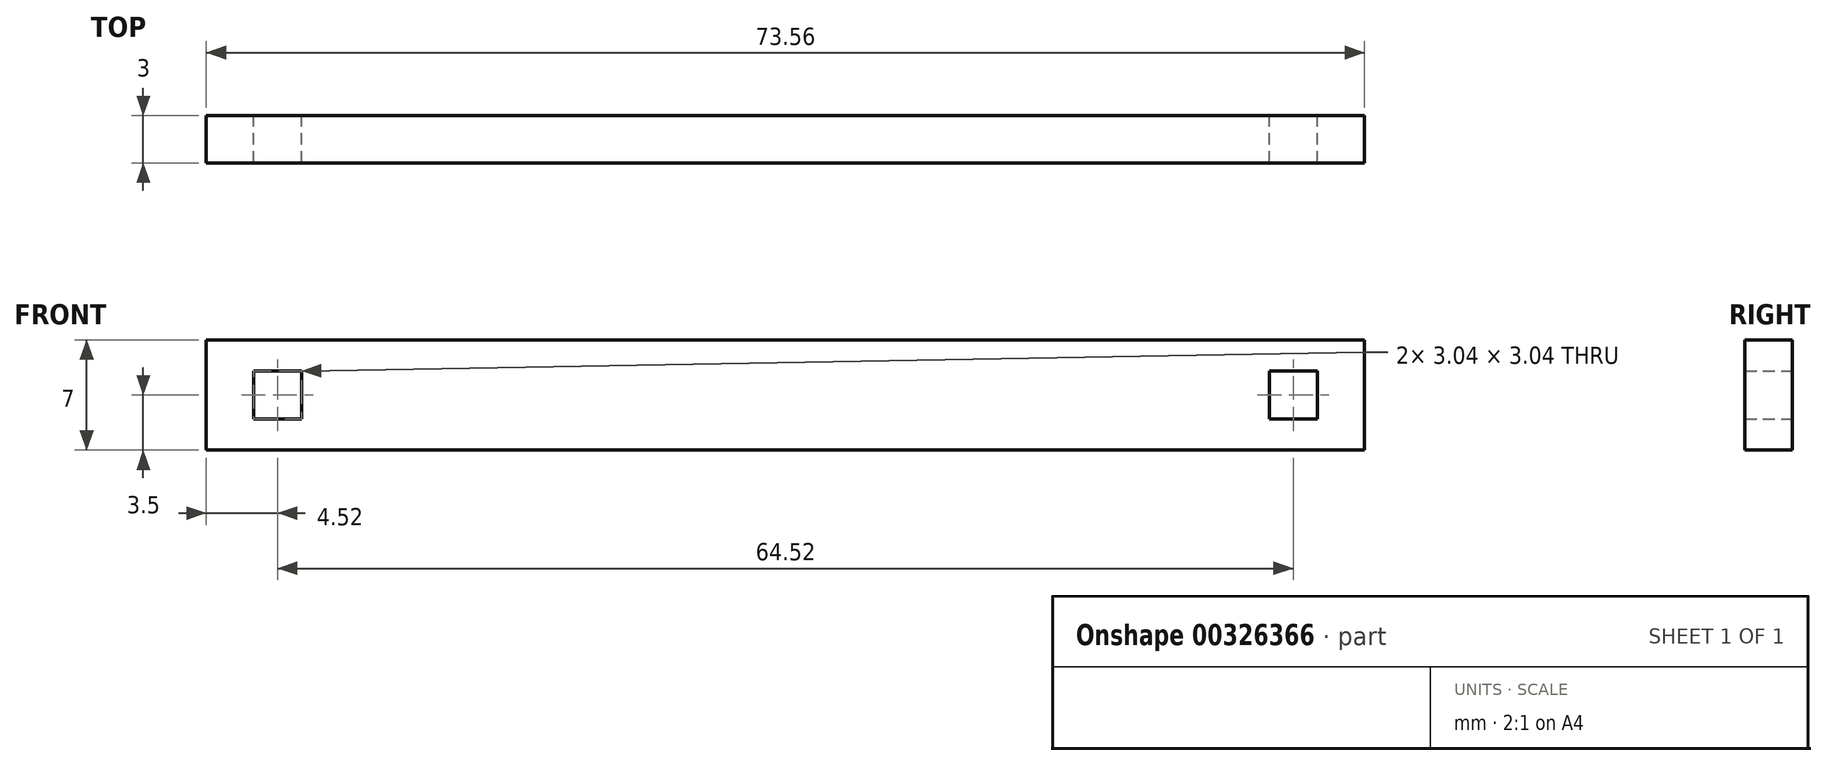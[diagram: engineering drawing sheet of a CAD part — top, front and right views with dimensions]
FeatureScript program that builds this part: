
annotation { "Feature Type Name" : "Feature", "Feature Type Description" : "" }
export const myFeature = defineFeature(function(context is Context, id is Id, definition is map)
    precondition{}
    {
        {
            var Q0;
            Q0=qCreatedBy(makeId("Front.planeOp"),FACE);
            var sketch = newSketch(context, id + "F0", { "sketchPlane" : qUnion([Q0])});
            skLineSegment(sketch, "E0", {"start": v(-36.78, 0) * mm, "end": v(36.78, 0) * mm});
            skLineSegment(sketch, "E1", {"start": v(36.78, 0) * mm, "end": v(36.78, 7) * mm});
            skLineSegment(sketch, "E2", {"start": v(36.78, 7) * mm, "end": v(-36.78, 7) * mm});
            skLineSegment(sketch, "E3", {"start": v(-36.78, 7) * mm, "end": v(-36.78, 0) * mm});
            skLineSegment(sketch, "E4.bottom", {"start": v(-33.78, 5.02) * mm, "end": v(-30.74, 5.02) * mm});
            skLineSegment(sketch, "E4.top", {"start": v(-33.78, 1.98) * mm, "end": v(-30.74, 1.98) * mm});
            skLineSegment(sketch, "E4.left", {"start": v(-33.78, 5.02) * mm, "end": v(-33.78, 1.98) * mm});
            skLineSegment(sketch, "E4.right", {"start": v(-30.74, 5.02) * mm, "end": v(-30.74, 1.98) * mm});
            skLineSegment(sketch, "E5.bottom", {"start": v(30.74, 5.02) * mm, "end": v(33.78, 5.02) * mm});
            skLineSegment(sketch, "E5.top", {"start": v(30.74, 1.98) * mm, "end": v(33.78, 1.98) * mm});
            skLineSegment(sketch, "E5.left", {"start": v(30.74, 5.02) * mm, "end": v(30.74, 1.98) * mm});
            skLineSegment(sketch, "E5.right", {"start": v(33.78, 5.02) * mm, "end": v(33.78, 1.98) * mm});
            skSolve(sketch);
        }
        {
            var Q0;
            Q0=makeQuery(id+"F0.imprint","IMPRINT",FACE,{"disambiguationData":[TD([[makeQuery(id+"F0.imprint","IMPRINT",EDGE,{"derivedFrom":sQuery(id+"F0.wireOp",EDGE,"E0")}),1.0]])]});
            extrude(context, id + "F1", {"entities" : qUnion([Q0]), "depth" : 3 * mm});
        }
    });
